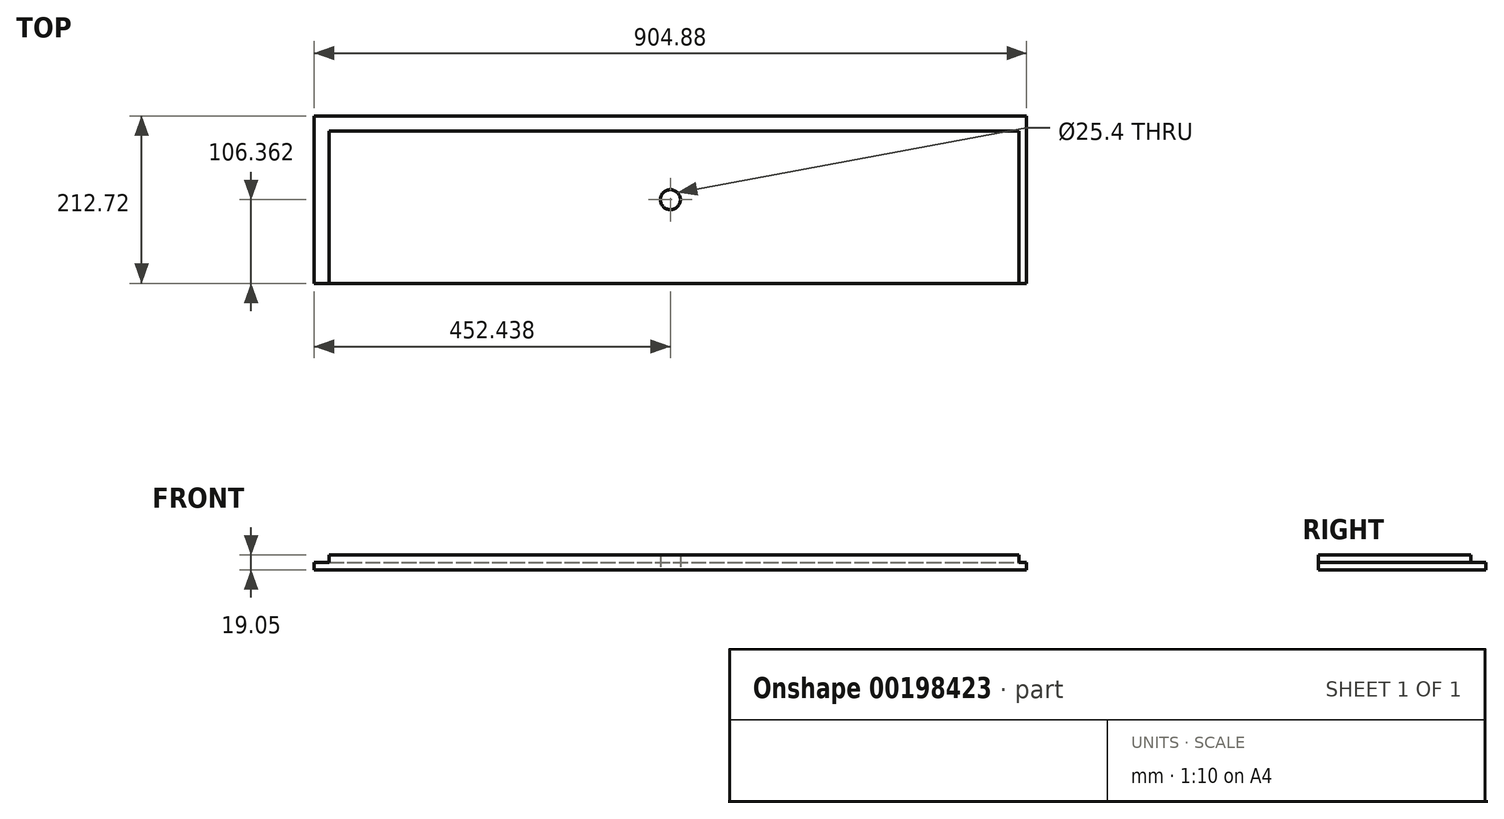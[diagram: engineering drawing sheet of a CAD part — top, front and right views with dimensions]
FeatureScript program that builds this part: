
annotation { "Feature Type Name" : "Feature", "Feature Type Description" : "" }
export const myFeature = defineFeature(function(context is Context, id is Id, definition is map)
    precondition{}
    {
        {
            var Q0;
            Q0=qCreatedBy(makeId("Top.planeOp"),FACE);
            var sketch = newSketch(context, id + "F0", { "sketchPlane" : qUnion([Q0])});
            skLineSegment(sketch, "E0.bottom", {"start": v(0, 0) * mm, "end": v(904.87, 0) * mm});
            skLineSegment(sketch, "E0.top", {"start": v(0, 212.73) * mm, "end": v(904.88, 212.73) * mm});
            skLineSegment(sketch, "E0.left", {"start": v(0, 0) * mm, "end": v(0, 212.73) * mm});
            skLineSegment(sketch, "E0.right", {"start": v(904.88, 0) * mm, "end": v(904.88, 212.73) * mm});
            skLineSegment(sketch, "E1.bottom", {"start": v(19.05, 193.68) * mm, "end": v(895.35, 193.68) * mm});
            skLineSegment(sketch, "E1.top", {"start": v(19.05, 0) * mm, "end": v(895.35, 0) * mm});
            skLineSegment(sketch, "E1.left", {"start": v(19.05, 193.68) * mm, "end": v(19.05, 0) * mm});
            skLineSegment(sketch, "E1.right", {"start": v(895.35, 193.68) * mm, "end": v(895.35, 0) * mm});
            skCircle(sketch, "E2", {"center": v(452.44, 106.36) * mm, "radius": 12.7 * mm});
            skSolve(sketch);
        }
        {
            var Q0;
            Q0=makeQuery(id+"F0.imprint","IMPRINT",FACE,{"disambiguationData":[TD([[makeQuery(id+"F0.imprint","IMPRINT",EDGE,{"derivedFrom":sQuery(id+"F0.wireOp",EDGE,"E1.bottom")}),-1.0]])]});
            extrude(context, id + "F1", {"entities" : qUnion([Q0]), "depth" : 19.05 * mm});
        }
        {
            var Q0;
            Q0=qSketchRegion(id+"F0",true);
            extrude(context, id + "F2", {"entities" : qUnion([Q0]), "operationType" : NewBodyOperationType.ADD, "depth" : 9.52 * mm});
        }
    });
